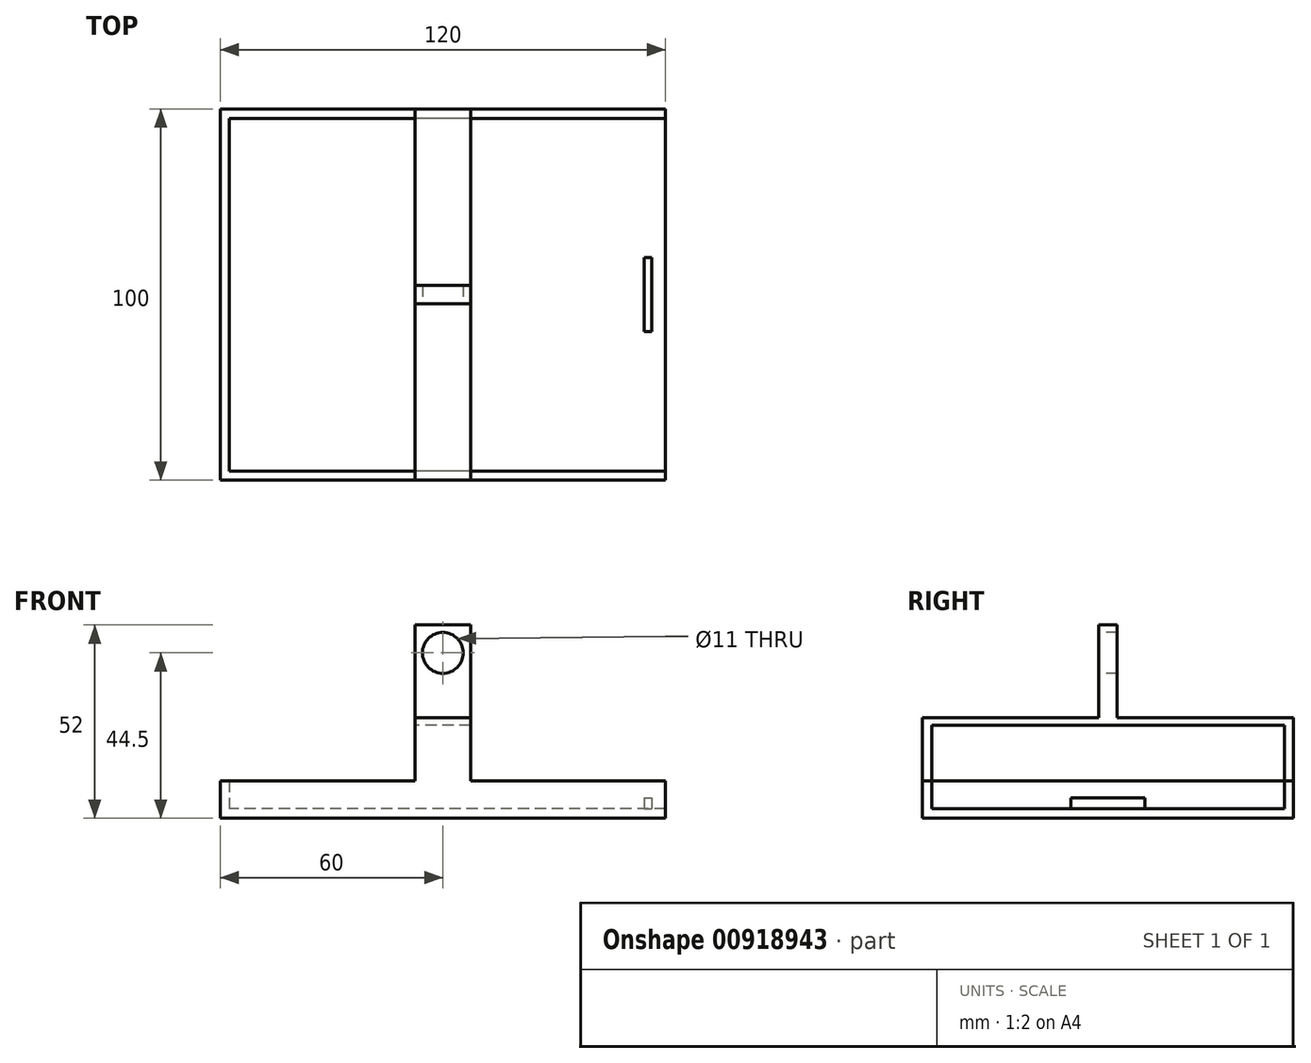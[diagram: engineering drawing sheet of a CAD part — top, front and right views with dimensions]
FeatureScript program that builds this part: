
annotation { "Feature Type Name" : "Feature", "Feature Type Description" : "" }
export const myFeature = defineFeature(function(context is Context, id is Id, definition is map)
    precondition{}
    {
        {
            var Q0;
            Q0=qCreatedBy(makeId("Top.planeOp"),FACE);
            var sketch = newSketch(context, id + "F0", { "sketchPlane" : qUnion([Q0])});
            skLineSegment(sketch, "E0.bottom", {"start": v(60, 50) * mm, "end": v(-60, 50) * mm});
            skLineSegment(sketch, "E0.top", {"start": v(60, -50) * mm, "end": v(-60, -50) * mm});
            skLineSegment(sketch, "E0.left", {"start": v(60, 50) * mm, "end": v(60, -50) * mm});
            skLineSegment(sketch, "E0.right", {"start": v(-60, 50) * mm, "end": v(-60, -50) * mm});
            skPoint(sketch, "E0.middle", {"position": v(0, 0) * mm});
            skSolve(sketch);
        }
        {
            var Q0;
            Q0=makeQuery(id+"F0.imprint","IMPRINT",FACE,{"disambiguationData":[TD([[makeQuery(id+"F0.imprint","IMPRINT",EDGE,{"derivedFrom":sQuery(id+"F0.wireOp",EDGE,"E0.bottom")}),1.0]])]});
            extrude(context, id + "F1", {"entities" : qUnion([Q0]), "depth" : 10 * mm, "offsetDistance" : 25 * mm});
        }
        {
            var Q0;
            Q0=makeQuery(id+"F1.opExtrude","CAP_FACE",FACE,{"disambiguationData":[OSD([sQuery(id+"F0.wireOp",EDGE,"E0.bottom"),sQuery(id+"F0.wireOp",EDGE,"E0.top"),sQuery(id+"F0.wireOp",EDGE,"E0.left"),sQuery(id+"F0.wireOp",EDGE,"E0.right")])],"isStart":false});
            shell(context, id + "F2", {"entities" : qUnion([Q0]), "thickness" : 2.5 * mm});
        }
        {
            var Q0;
            Q0=makeQuery(id+"F2.opShell","OFFSET_FACE",FACE,{"disambiguationData":[OSD([sQuery(id+"F0.wireOp",EDGE,"E0.bottom"),sQuery(id+"F0.wireOp",EDGE,"E0.top"),sQuery(id+"F0.wireOp",EDGE,"E0.left"),sQuery(id+"F0.wireOp",EDGE,"E0.right")])]});
            var sketch = newSketch(context, id + "F3", { "sketchPlane" : qUnion([Q0])});
            skSolve(sketch);
        }
        {
            var Q0;
            {var subQ0=sQuery(id+"F0.wireOp",EDGE,"E0.bottom");Q0=makeQuery(id+"F3.imprint","IMPRINT",FACE,{"disambiguationData":[TD([[makeQuery(id+"F3.imprint","IMPRINT",EDGE,{"derivedFrom":makeQuery(id+"F2.opShell","OFFSET_EDGE",EDGE,{"disambiguationData":[OSD([subQ0]),TDD([makeQuery(id+"F1.opExtrude","CAP_EDGE",EDGE,{"disambiguationData":[OSD([subQ0])],"isStart":true})])]})}),1.0]])]});}
            var sketch = newSketch(context, id + "F4", { "sketchPlane" : qUnion([Q0])});
            skLineSegment(sketch, "E1.bottom", {"start": v(57.25, 47.5) * mm, "end": v(60.25, 47.5) * mm});
            skLineSegment(sketch, "E1.top", {"start": v(57.25, -47.5) * mm, "end": v(60.25, -47.5) * mm});
            skLineSegment(sketch, "E1.left", {"start": v(57.25, 47.5) * mm, "end": v(57.25, -47.5) * mm});
            skLineSegment(sketch, "E1.right", {"start": v(60.25, 47.5) * mm, "end": v(60.25, -47.5) * mm});
            skPoint(sketch, "E1.middle", {"position": v(58.75, 0) * mm});
            skLineSegment(sketch, "E2.bottom", {"start": v(54.27, 10) * mm, "end": v(56.27, 10) * mm});
            skLineSegment(sketch, "E2.top", {"start": v(54.27, -10) * mm, "end": v(56.27, -10) * mm});
            skLineSegment(sketch, "E2.left", {"start": v(54.27, 10) * mm, "end": v(54.27, -10) * mm});
            skLineSegment(sketch, "E2.right", {"start": v(56.27, 10) * mm, "end": v(56.27, -10) * mm});
            skPoint(sketch, "E2.middle", {"position": v(55.27, 0) * mm});
            skSolve(sketch);
        }
        {
            var Q0;
            Q0=makeQuery(id+"F4.imprint","IMPRINT",FACE,{"disambiguationData":[TD([[makeQuery(id+"F4.imprint","IMPRINT",EDGE,{"derivedFrom":sQuery(id+"F4.wireOp",EDGE,"E1.bottom")}),-1.0]])]});
            extrude(context, id + "F5", {"entities" : qUnion([Q0]), "operationType" : NewBodyOperationType.REMOVE, "depth" : 10 * mm, "offsetDistance" : 25 * mm});
        }
        {
            var Q0;
            Q0=makeQuery(id+"F1.opExtrude","CAP_FACE",FACE,{"disambiguationData":[OSD([sQuery(id+"F0.wireOp",EDGE,"E0.bottom"),sQuery(id+"F0.wireOp",EDGE,"E0.top"),sQuery(id+"F0.wireOp",EDGE,"E0.left"),sQuery(id+"F0.wireOp",EDGE,"E0.right")])],"isStart":false});
            var sketch = newSketch(context, id + "F6", { "sketchPlane" : qUnion([Q0])});
            skLineSegment(sketch, "E3.bottom", {"start": v(-7.5, -50) * mm, "end": v(7.5, -50) * mm});
            skLineSegment(sketch, "E3.top", {"start": v(-7.5, -47.5) * mm, "end": v(7.5, -47.5) * mm});
            skLineSegment(sketch, "E3.left", {"start": v(-7.5, -50) * mm, "end": v(-7.5, -47.5) * mm});
            skLineSegment(sketch, "E3.right", {"start": v(7.5, -50) * mm, "end": v(7.5, -47.5) * mm});
            skPoint(sketch, "E3.middle", {"position": v(0, -48.75) * mm});
            skLineSegment(sketch, "E4.bottom", {"start": v(-7.5, 47.5) * mm, "end": v(7.5, 47.5) * mm});
            skLineSegment(sketch, "E4.top", {"start": v(-7.5, 50) * mm, "end": v(7.5, 50) * mm});
            skLineSegment(sketch, "E4.left", {"start": v(-7.5, 47.5) * mm, "end": v(-7.5, 50) * mm});
            skLineSegment(sketch, "E4.right", {"start": v(7.5, 47.5) * mm, "end": v(7.5, 50) * mm});
            skPoint(sketch, "E4.middle", {"position": v(0, 48.75) * mm});
            skSolve(sketch);
        }
        {
            var Q0;
            Q0=makeQuery(id+"F6.imprint","IMPRINT",FACE,{"disambiguationData":[TD([[makeQuery(id+"F6.imprint","IMPRINT",EDGE,{"derivedFrom":sQuery(id+"F6.wireOp",EDGE,"E3.bottom")}),-1.0]])]});
            var Q1;
            Q1=makeQuery(id+"F6.imprint","IMPRINT",FACE,{"disambiguationData":[TD([[makeQuery(id+"F6.imprint","IMPRINT",EDGE,{"derivedFrom":sQuery(id+"F6.wireOp",EDGE,"E4.bottom")}),-1.0]])]});
            extrude(context, id + "F7", {"entities" : qUnion([Q0, Q1]), "operationType" : NewBodyOperationType.ADD, "depth" : 15 * mm, "offsetDistance" : 25 * mm});
        }
        {
            var Q0;
            Q0=makeQuery(id+"F7.opExtrude","CAP_FACE",FACE,{"disambiguationData":[OSD([sQuery(id+"F6.wireOp",EDGE,"E3.bottom"),sQuery(id+"F6.wireOp",EDGE,"E3.top"),sQuery(id+"F6.wireOp",EDGE,"E3.left"),sQuery(id+"F6.wireOp",EDGE,"E3.right")])],"isStart":false});
            var sketch = newSketch(context, id + "F8", { "sketchPlane" : qUnion([Q0])});
            skLineSegment(sketch, "E5.bottom", {"start": v(-7.5, -50) * mm, "end": v(7.5, -50) * mm});
            skLineSegment(sketch, "E5.top", {"start": v(-7.5, 50) * mm, "end": v(7.5, 50) * mm});
            skLineSegment(sketch, "E5.left", {"start": v(-7.5, -50) * mm, "end": v(-7.5, 50) * mm});
            skLineSegment(sketch, "E5.right", {"start": v(7.5, -50) * mm, "end": v(7.5, 50) * mm});
            skPoint(sketch, "E5.middle", {"position": v(0, 0) * mm});
            skSolve(sketch);
        }
        {
            var Q0;
            {var subQ0=sQuery(id+"F8.wireOp",EDGE,"E5.bottom");Q0=makeQuery(id+"F8.imprint","IMPRINT",FACE,{"disambiguationData":[TD([[makeQuery(id+"F8.imprint","IMPRINT",EDGE,{"derivedFrom":subQ0}),-1.0]])]});}
            var Q1;
            {var subQ0=sQuery(id+"F8.wireOp",EDGE,"E5.top");Q1=makeQuery(id+"F8.imprint","IMPRINT",FACE,{"disambiguationData":[TD([[makeQuery(id+"F8.imprint","IMPRINT",EDGE,{"derivedFrom":subQ0}),-1.0]])]});}
            extrude(context, id + "F9", {"entities" : qUnion([Q0, Q1]), "operationType" : NewBodyOperationType.ADD, "depth" : 2 * mm, "offsetDistance" : 25 * mm});
        }
        {
            var Q0;
            Q0=makeQuery(id+"F9.opExtrude","CAP_FACE",FACE,{"disambiguationData":[OSD([sQuery(id+"F8.wireOp",EDGE,"E5.bottom"),sQuery(id+"F8.wireOp",EDGE,"E5.top"),sQuery(id+"F8.wireOp",EDGE,"E5.left"),sQuery(id+"F8.wireOp",EDGE,"E5.right")])],"isStart":false});
            var sketch = newSketch(context, id + "F10", { "sketchPlane" : qUnion([Q0])});
            skLineSegment(sketch, "E6.bottom", {"start": v(-7.5, -2.5) * mm, "end": v(7.5, -2.5) * mm});
            skLineSegment(sketch, "E6.top", {"start": v(-7.5, 2.5) * mm, "end": v(7.5, 2.5) * mm});
            skLineSegment(sketch, "E6.left", {"start": v(-7.5, -2.5) * mm, "end": v(-7.5, 2.5) * mm});
            skLineSegment(sketch, "E6.right", {"start": v(7.5, -2.5) * mm, "end": v(7.5, 2.5) * mm});
            skPoint(sketch, "E6.middle", {"position": v(0, 0) * mm});
            skSolve(sketch);
        }
        {
            var Q0;
            Q0=makeQuery(id+"F10.imprint","IMPRINT",FACE,{"disambiguationData":[TD([[makeQuery(id+"F10.imprint","IMPRINT",EDGE,{"derivedFrom":sQuery(id+"F10.wireOp",EDGE,"E6.bottom")}),1.0]])]});
            extrude(context, id + "F11", {"entities" : qUnion([Q0]), "operationType" : NewBodyOperationType.ADD, "depth" : 25 * mm, "offsetDistance" : 25 * mm});
        }
        {
            var Q0;
            Q0=makeQuery(id+"F11.opExtrude","SWEPT_FACE",FACE,{"disambiguationData":[OSD([sQuery(id+"F10.wireOp",EDGE,"E6.bottom")])]});
            var sketch = newSketch(context, id + "F12", { "sketchPlane" : qUnion([Q0])});
            skCircle(sketch, "E7", {"center": v(0, 44.5) * mm, "radius": 5.5 * mm});
            skSolve(sketch);
        }
        {
            var Q0;
            Q0 = qSketchRegion(id + "F12", true);
            extrude(context, id + "F13", {"entities" : qUnion([Q0]), "operationType" : NewBodyOperationType.REMOVE, "endBound" : BoundingType.UP_TO_NEXT, "oppositeDirection" : true, "depth" : 25 * mm, "offsetDistance" : 25 * mm});
        }
        {
            var Q0;
            Q0=makeQuery(id+"F4.imprint","IMPRINT",FACE,{"disambiguationData":[TD([[makeQuery(id+"F4.imprint","IMPRINT",EDGE,{"derivedFrom":sQuery(id+"F4.wireOp",EDGE,"E2.bottom")}),-1.0]])]});
            extrude(context, id + "F14", {"entities" : qUnion([Q0]), "operationType" : NewBodyOperationType.ADD, "depth" : 3 * mm, "offsetDistance" : 25 * mm});
        }
    });
